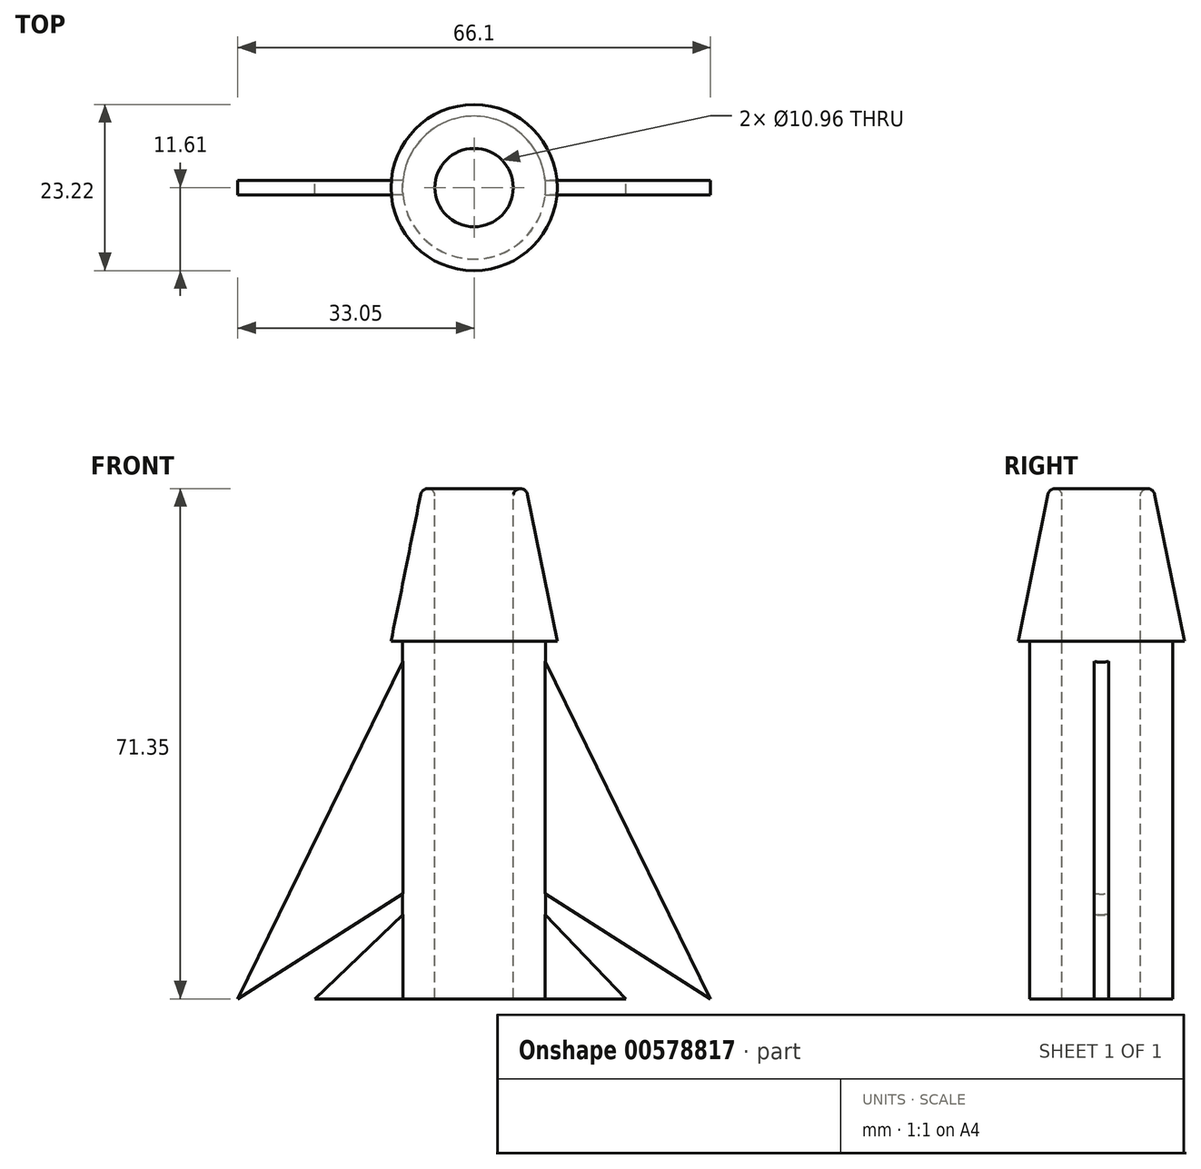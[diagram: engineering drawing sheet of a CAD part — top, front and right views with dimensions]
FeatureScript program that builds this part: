
annotation { "Feature Type Name" : "Feature", "Feature Type Description" : "" }
export const myFeature = defineFeature(function(context is Context, id is Id, definition is map)
    precondition{}
    {
        {
            var Q0;
            Q0=qCreatedBy(makeId("Top.planeOp"),FACE);
            var sketch = newSketch(context, id + "F0", { "sketchPlane" : qUnion([Q0])});
            skCircle(sketch, "E0", {"center": v(0, 0) * mm, "radius": 10 * mm});
            skSolve(sketch);
        }
        {
            var Q0;
            Q0=makeQuery(id+"F0.imprint","IMPRINT",FACE,{"disambiguationData":[TD([[makeQuery(id+"F0.imprint","IMPRINT",EDGE,{"derivedFrom":sQuery(id+"F0.wireOp",EDGE,"E0")}),1.0]])]});
            extrude(context, id + "F1", {"entities" : qUnion([Q0]), "depth" : 50 * mm, "offsetDistance" : 25 * mm});
        }
        {
            var Q0;
            Q0=qCreatedBy(makeId("Right.planeOp"),FACE);
            var sketch = newSketch(context, id + "F2", { "sketchPlane" : qUnion([Q0])});
            skLineSegment(sketch, "E1", {"start": v(11.61, 50) * mm, "end": v(-11.85, 50) * mm});
            skLineSegment(sketch, "E2", {"start": v(-11.85, 50) * mm, "end": v(0, 107.48) * mm});
            skLineSegment(sketch, "E3", {"start": v(0, 107.48) * mm, "end": v(11.61, 50) * mm});
            skLineSegment(sketch, "E4", {"start": v(0, 50) * mm, "end": v(0, 107.48) * mm});
            skSolve(sketch);
        }
        {
            var Q0;
            {var subQ0=sQuery(id+"F2.wireOp",EDGE,"E3");Q0=makeQuery(id+"F2.imprint","IMPRINT",FACE,{"disambiguationData":[TD([[makeQuery(id+"F2.imprint","IMPRINT",EDGE,{"derivedFrom":subQ0}),-1.0]])]});}
            var Q1;
            Q1=sQuery(id+"F2.wireOp",EDGE,"E4");
            revolve(context, id + "F3", {"entities" : qUnion([Q0]), "axis" : qUnion([Q1]), "revolveType" : RevolveType.FULL});
        }
        {
            var Q0;
            Q0=qCreatedBy(makeId("Front.planeOp"),FACE);
            var sketch = newSketch(context, id + "F4", { "sketchPlane" : qUnion([Q0])});
            skLineSegment(sketch, "E5", {"start": v(9.08, 48.98) * mm, "end": v(33.05, 0) * mm});
            skLineSegment(sketch, "E6", {"start": v(33.05, 0) * mm, "end": v(9.37, 15.08) * mm});
            skLineSegment(sketch, "E7", {"start": v(-9.08, 48.98) * mm, "end": v(-33.05, 0) * mm});
            skLineSegment(sketch, "E8", {"start": v(-9.37, 15.08) * mm, "end": v(-33.05, 0) * mm});
            skLineSegment(sketch, "E9", {"start": v(9.08, 48.98) * mm, "end": v(9.37, 15.08) * mm});
            skLineSegment(sketch, "E10", {"start": v(-9.37, 15.08) * mm, "end": v(-9.08, 48.98) * mm});
            skLineSegment(sketch, "E11", {"start": v(9.89, 11.85) * mm, "end": v(21.26, 0) * mm});
            skLineSegment(sketch, "E12", {"start": v(21.26, 0) * mm, "end": v(9.89, 0) * mm});
            skLineSegment(sketch, "E13", {"start": v(9.89, 0) * mm, "end": v(9.89, 11.85) * mm});
            skLineSegment(sketch, "E14", {"start": v(-22.28, 0) * mm, "end": v(-9.89, 11.85) * mm});
            skLineSegment(sketch, "E15", {"start": v(-9.89, 11.85) * mm, "end": v(-9.89, 0) * mm});
            skLineSegment(sketch, "E16", {"start": v(-9.89, 0) * mm, "end": v(-22.28, 0) * mm});
            skSolve(sketch);
        }
        {
            var Q0;
            Q0=makeQuery(id+"F4.imprint","IMPRINT",FACE,{"disambiguationData":[TD([[makeQuery(id+"F4.imprint","IMPRINT",EDGE,{"derivedFrom":sQuery(id+"F4.wireOp",EDGE,"E7")}),1.0]])]});
            var Q1;
            Q1=makeQuery(id+"F4.imprint","IMPRINT",FACE,{"disambiguationData":[TD([[makeQuery(id+"F4.imprint","IMPRINT",EDGE,{"derivedFrom":sQuery(id+"F4.wireOp",EDGE,"E5")}),-1.0]])]});
            var Q2;
            Q2=makeQuery(id+"F4.imprint","IMPRINT",FACE,{"disambiguationData":[TD([[makeQuery(id+"F4.imprint","IMPRINT",EDGE,{"derivedFrom":sQuery(id+"F4.wireOp",EDGE,"E14")}),-1.0]])]});
            var Q3;
            Q3=makeQuery(id+"F4.imprint","IMPRINT",FACE,{"disambiguationData":[TD([[makeQuery(id+"F4.imprint","IMPRINT",EDGE,{"derivedFrom":sQuery(id+"F4.wireOp",EDGE,"E11")}),-1.0]])]});
            extrude(context, id + "F5", {"entities" : qUnion([Q0, Q1, Q2, Q3]), "operationType" : NewBodyOperationType.ADD, "endBound" : BoundingType.SYMMETRIC, "depth" : 2 * mm, "offsetDistance" : 25 * mm});
        }
        {
            var Q0;
            Q0=qCreatedBy(makeId("Top.planeOp"),FACE);
            var Q1;
            Q1=makeQuery(id+"F3.opRevolve","SWEPT_VERTEX",VERTEX,{"disambiguationData":[OSD([sQuery(id+"F2.wireOp",EDGE,"E2"),sQuery(id+"F2.wireOp",EDGE,"E3"),sQuery(id+"F2.wireOp",EDGE,"E4")])]});
            cPlane(context, id + "F6", {"entities" : qUnion([Q0, Q1]), "cplaneType" : CPlaneType.PLANE_POINT, "offset" : 25 * mm, "width" : 150 * mm, "height" : 150 * mm});
        }
        {
            var Q0;
            Q0=qCreatedBy(id+"F6.planeOp",FACE);
            var sketch = newSketch(context, id + "F7", { "sketchPlane" : qUnion([Q0])});
            skCircle(sketch, "E17", {"center": v(0, 0) * mm, "radius": 5.48 * mm});
            skSolve(sketch);
        }
        {
            var Q0;
            Q0 = qSketchRegion(id + "F7", true);
            extrude(context, id + "F8", {"entities" : qUnion([Q0]), "operationType" : NewBodyOperationType.REMOVE, "endBound" : BoundingType.THROUGH_ALL, "oppositeDirection" : true, "depth" : 25 * mm, "offsetDistance" : 25 * mm});
        }
        {
            var Q0;
            Q0=makeQuery(id+"F8.boolean.opBoolean","INTERSECT",EDGE,{"derivedFrom":[makeQuery(id+"F3.opRevolve","SWEPT_FACE",FACE,{"disambiguationData":[OSD([sQuery(id+"F2.wireOp",EDGE,"E3")])]}),makeQuery(id+"F8.opExtrude","SWEPT_FACE",FACE,{"disambiguationData":[OSD([sQuery(id+"F7.wireOp",EDGE,"E17")])]})]});
            fillet(context, id + "F9", {"entities" : qUnion([Q0]), "radius" : 1 * mm, "tangentPropagation" : true, "allowEdgeOverflow" : false});
        }
    });
